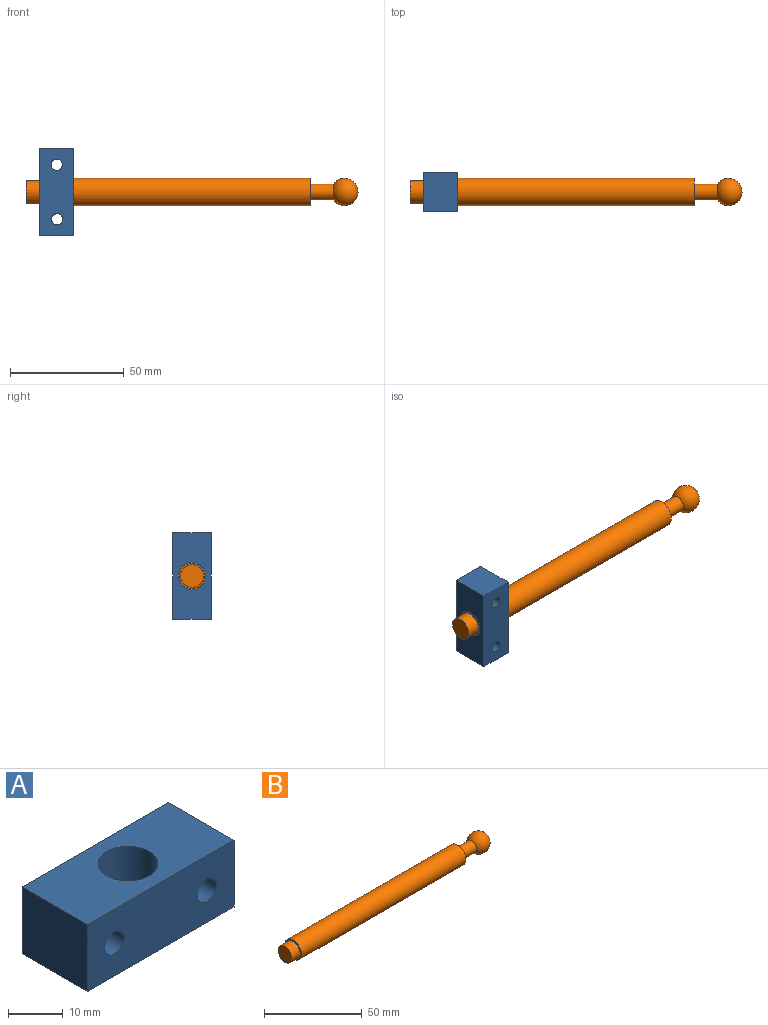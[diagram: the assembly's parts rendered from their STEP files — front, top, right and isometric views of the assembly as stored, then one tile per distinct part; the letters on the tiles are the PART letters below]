
ASSEMBLY  parts=2 mates=1
PART A: 9 faces, bbox 38x17x15 mm
  f0: plane 38x15mm, normal (0,-1,0), area 530.7mm2, adj f1,f3,f4,f5,f7,f8
  f1: plane 17x15mm, normal (1,0,0), area 255mm2, adj f0,f2,f4,f5
  f2: plane 38x15mm, normal (0,1,0), area 530.7mm2, adj f1,f3,f4,f5,f7,f8
  f3: plane 17x15mm, normal (-1,0,0), area 255mm2, adj f0,f2,f4,f5
  f4: plane 38x17mm, normal (0,0,1), area 551mm2, adj f0,f1,f2,f3,f6
  f5: plane 38x17mm, normal (0,0,-1), area 551mm2, adj f0,f1,f2,f3,f6
  f6: cylinder r=5.5mm len=15mm, axis (0,0,-1), area 518.4mm2, adj f4,f5
  f7: cylinder r=2.5mm len=17mm, axis (0,-1,0), area 267mm2, adj f0,f2
  f8: cylinder r=2.5mm len=17mm, axis (0,-1,0), area 267mm2, adj f0,f2
PART B: 7 faces, bbox 146x12x12 mm
  f0: cylinder r=3.5mm len=10.13mm, axis (-1,0,0), area 222.7mm2, adj f2,f6
  f1: cylinder r=6mm len=119mm, axis (-1,0,0), area 4486.2mm2, adj f2,f3
  f2: plane 12x12mm, normal (1,0,0), area 74.6mm2, adj f0,f1
  f3: plane 12x12mm, normal (-1,0,0), area 34.6mm2, adj f1,f4
  f4: cylinder r=5mm len=10mm, axis (1,0,0), area 188.5mm2, adj f3,f5
  f5: plane 10x10mm, normal (-1,0,0), area 78.5mm2, adj f4
  f6: sphere r=6mm, area 409.9mm2, adj f0
PLACE A rot(axis=(0.71,0,-0.71),180deg) t=(15,0,0)mm
PLACE B at identity
MATE slider A.f6 <-> B.f0  axis (-1,0,0) through (0,0,0)mm
